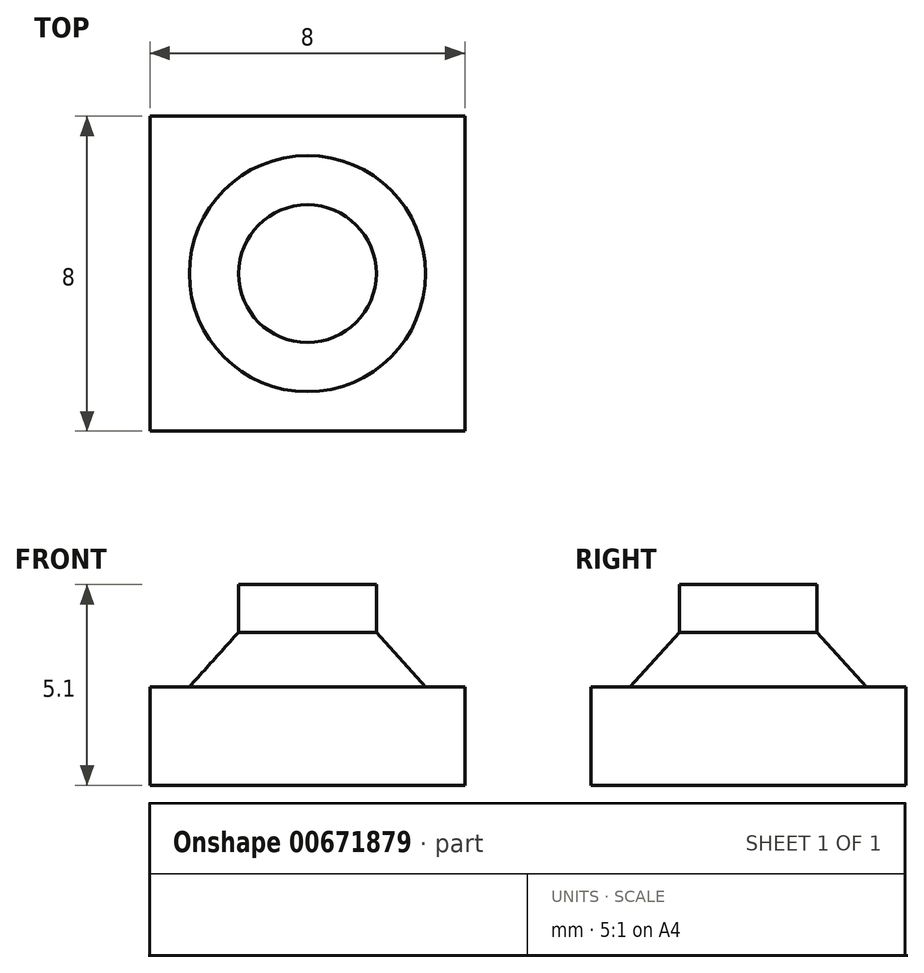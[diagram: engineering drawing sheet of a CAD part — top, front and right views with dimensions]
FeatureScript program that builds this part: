
annotation { "Feature Type Name" : "Feature", "Feature Type Description" : "" }
export const myFeature = defineFeature(function(context is Context, id is Id, definition is map)
    precondition{}
    {
        {
            var Q0;
            Q0=qCreatedBy(makeId("Top.planeOp"),FACE);
            var sketch = newSketch(context, id + "F0", { "sketchPlane" : qUnion([Q0])});
            skLineSegment(sketch, "E0.bottom", {"start": v(-4, 4) * mm, "end": v(4, 4) * mm});
            skLineSegment(sketch, "E0.top", {"start": v(-4, -4) * mm, "end": v(4, -4) * mm});
            skLineSegment(sketch, "E0.left", {"start": v(-4, 4) * mm, "end": v(-4, -4) * mm});
            skLineSegment(sketch, "E0.right", {"start": v(4, 4) * mm, "end": v(4, -4) * mm});
            skPoint(sketch, "E0.middle", {"position": v(0, 0) * mm});
            skSolve(sketch);
        }
        {
            var Q0;
            Q0 = qSketchRegion(id + "F0", true);
            extrude(context, id + "F1", {"entities" : qUnion([Q0]), "depth" : 2.5 * mm, "offsetDistance" : 25 * mm});
        }
        {
            var Q0;
            Q0=qCreatedBy(makeId("Front.planeOp"),FACE);
            var sketch = newSketch(context, id + "F2", { "sketchPlane" : qUnion([Q0])});
            skLineSegment(sketch, "E1.0.1", {"start": v(-4, 2.5) * mm, "end": v(4, 2.5) * mm});
            skLineSegment(sketch, "E1.0.3", {"start": v(4, 2.5) * mm, "end": v(-4, 2.5) * mm});
            skLineSegment(sketch, "E2", {"start": v(0, 2.5) * mm, "end": v(0, 5.1) * mm});
            skLineSegment(sketch, "E3", {"start": v(0, 5.1) * mm, "end": v(1.75, 5.1) * mm});
            skLineSegment(sketch, "E4", {"start": v(1.75, 5.1) * mm, "end": v(1.75, 3.9) * mm});
            skLineSegment(sketch, "E5", {"start": v(1.75, 3.9) * mm, "end": v(3, 2.5) * mm});
            skSolve(sketch);
        }
        {
            var Q0;
            {var subQ0=sQuery(id+"F2.wireOp",EDGE,"E2");Q0=makeQuery(id+"F2.imprint","IMPRINT",FACE,{"disambiguationData":[TD([[makeQuery(id+"F2.imprint","IMPRINT",EDGE,{"derivedFrom":subQ0}),-1.0]])]});}
            var Q1;
            Q1=sQuery(id+"F2.wireOp",EDGE,"E2");
            revolve(context, id + "F3", {"operationType" : NewBodyOperationType.ADD, "entities" : qUnion([Q0]), "axis" : qUnion([Q1]), "revolveType" : RevolveType.FULL});
        }
    });
